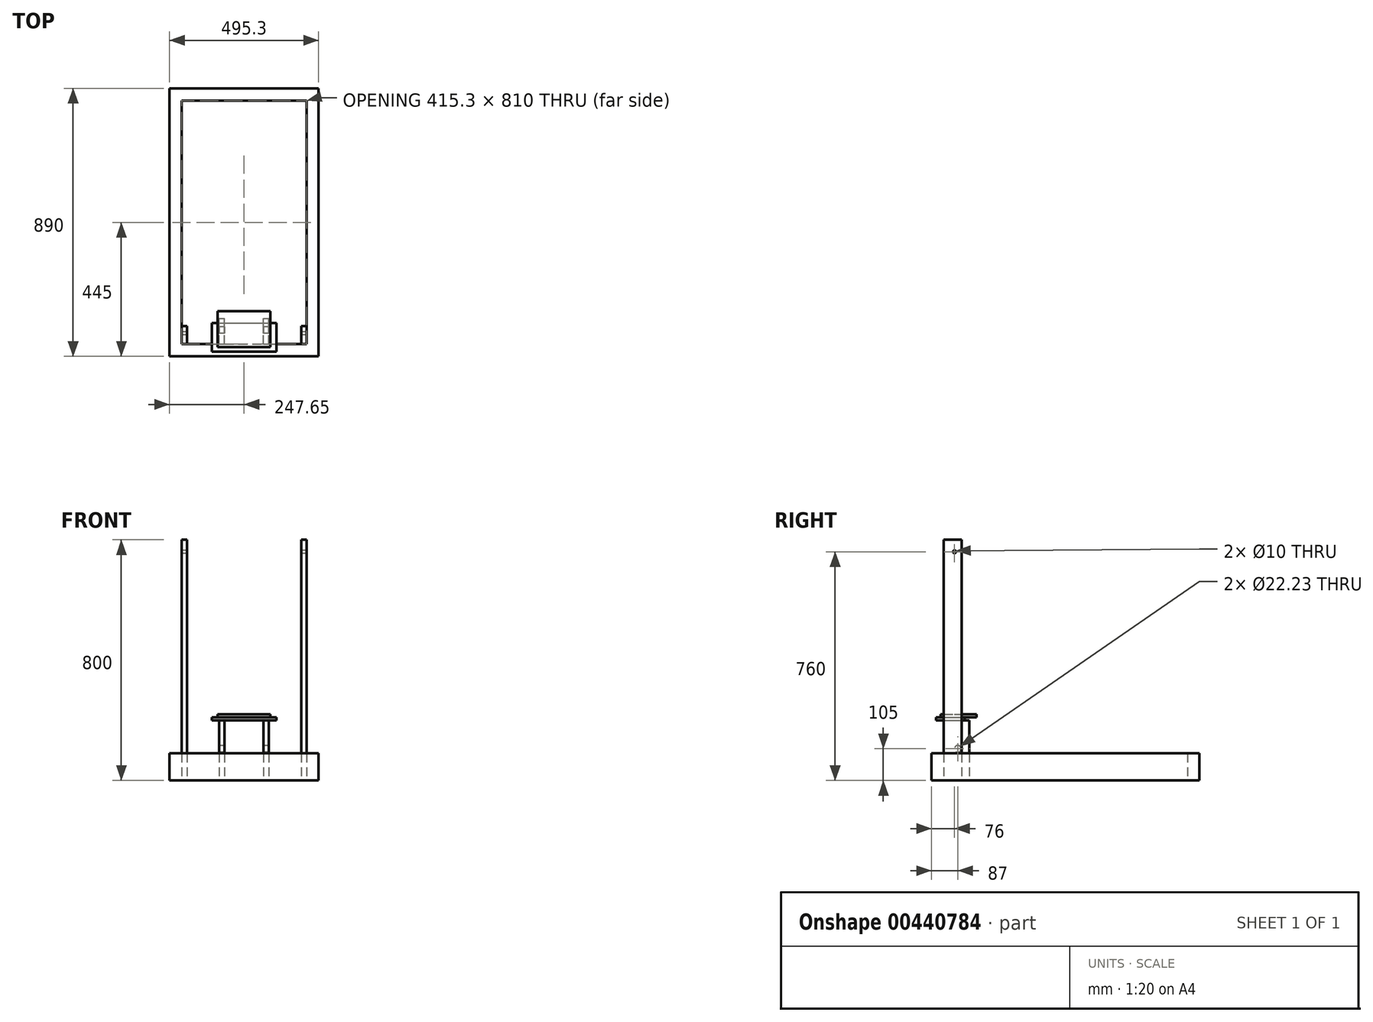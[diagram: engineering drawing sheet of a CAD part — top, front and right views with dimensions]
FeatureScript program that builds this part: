
annotation { "Feature Type Name" : "Feature", "Feature Type Description" : "" }
export const myFeature = defineFeature(function(context is Context, id is Id, definition is map)
    precondition{}
    {
        {
            var Q0;
            Q0=qCreatedBy(makeId("Top.planeOp"),FACE);
            var sketch = newSketch(context, id + "F0", { "sketchPlane" : qUnion([Q0])});
            skLineSegment(sketch, "E0.bottom", {"start": v(0, 0) * mm, "end": v(495.3, 0) * mm});
            skLineSegment(sketch, "E0.top", {"start": v(0, 890) * mm, "end": v(495.3, 890) * mm});
            skLineSegment(sketch, "E0.left", {"start": v(0, 0) * mm, "end": v(0, 890) * mm});
            skLineSegment(sketch, "E0.right", {"start": v(495.3, 0) * mm, "end": v(495.3, 890) * mm});
            skLineSegment(sketch, "E1.bottom", {"start": v(40, 40) * mm, "end": v(455.3, 40) * mm});
            skLineSegment(sketch, "E1.top", {"start": v(40, 850) * mm, "end": v(455.3, 850) * mm});
            skLineSegment(sketch, "E1.left", {"start": v(40, 40) * mm, "end": v(40, 850) * mm});
            skLineSegment(sketch, "E1.right", {"start": v(455.3, 40) * mm, "end": v(455.3, 850) * mm});
            skSolve(sketch);
        }
        {
            var Q0;
            Q0 = qSketchRegion(id + "F0", true);
            extrude(context, id + "F1", {"entities" : qUnion([Q0]), "depth" : 90 * mm});
        }
        {
            var Q0;
            Q0=qCreatedBy(makeId("Top.planeOp"),FACE);
            var sketch = newSketch(context, id + "F2", { "sketchPlane" : qUnion([Q0])});
            skLineSegment(sketch, "E2.bottom", {"start": v(165, 40) * mm, "end": v(182.5, 40) * mm});
            skLineSegment(sketch, "E2.top", {"start": v(165, 125) * mm, "end": v(182.5, 125) * mm});
            skLineSegment(sketch, "E2.left", {"start": v(165, 40) * mm, "end": v(165, 125) * mm});
            skLineSegment(sketch, "E2.right", {"start": v(182.5, 40) * mm, "end": v(182.5, 125) * mm});
            skLineSegment(sketch, "E3.bottom", {"start": v(312.3, 40) * mm, "end": v(330.3, 40) * mm});
            skLineSegment(sketch, "E3.top", {"start": v(312.3, 125) * mm, "end": v(330.3, 125) * mm});
            skLineSegment(sketch, "E3.left", {"start": v(330.3, 40) * mm, "end": v(330.3, 125) * mm});
            skLineSegment(sketch, "E3.right", {"start": v(312.3, 40) * mm, "end": v(312.3, 125) * mm});
            skSolve(sketch);
        }
        {
            var Q0;
            Q0=makeQuery(id+"F2.imprint","IMPRINT",FACE,{"disambiguationData":[TD([[makeQuery(id+"F2.imprint","IMPRINT",EDGE,{"derivedFrom":sQuery(id+"F2.wireOp",EDGE,"E2.bottom")}),1.0]])]});
            var Q1;
            Q1=makeQuery(id+"F2.imprint","IMPRINT",FACE,{"disambiguationData":[TD([[makeQuery(id+"F2.imprint","IMPRINT",EDGE,{"derivedFrom":sQuery(id+"F2.wireOp",EDGE,"E3.bottom")}),1.0]])]});
            extrude(context, id + "F3", {"entities" : qUnion([Q0, Q1]), "operationType" : NewBodyOperationType.ADD, "depth" : 200 * mm});
        }
        {
            var Q0;
            Q0=qCreatedBy(makeId("Top.planeOp"),FACE);
            var sketch = newSketch(context, id + "F4", { "sketchPlane" : qUnion([Q0])});
            skLineSegment(sketch, "E4.bottom", {"start": v(40, 40) * mm, "end": v(57.5, 40) * mm});
            skLineSegment(sketch, "E4.top", {"start": v(40, 100) * mm, "end": v(57.5, 100) * mm});
            skLineSegment(sketch, "E4.left", {"start": v(40, 40) * mm, "end": v(40, 100) * mm});
            skLineSegment(sketch, "E4.right", {"start": v(57.5, 40) * mm, "end": v(57.5, 100) * mm});
            skLineSegment(sketch, "E5.bottom", {"start": v(437.3, 40) * mm, "end": v(455.3, 40) * mm});
            skLineSegment(sketch, "E5.top", {"start": v(437.3, 100) * mm, "end": v(455.3, 100) * mm});
            skLineSegment(sketch, "E5.left", {"start": v(437.3, 40) * mm, "end": v(437.3, 100) * mm});
            skLineSegment(sketch, "E5.right", {"start": v(455.3, 40) * mm, "end": v(455.3, 100) * mm});
            skSolve(sketch);
        }
        {
            var Q0;
            Q0=makeQuery(id+"F4.imprint","IMPRINT",FACE,{"disambiguationData":[TD([[makeQuery(id+"F4.imprint","IMPRINT",EDGE,{"derivedFrom":sQuery(id+"F4.wireOp",EDGE,"E4.bottom")}),1.0]])]});
            var Q1;
            Q1=makeQuery(id+"F4.imprint","IMPRINT",FACE,{"disambiguationData":[TD([[makeQuery(id+"F4.imprint","IMPRINT",EDGE,{"derivedFrom":sQuery(id+"F4.wireOp",EDGE,"E5.bottom")}),1.0]])]});
            extrude(context, id + "F5", {"entities" : qUnion([Q0, Q1]), "operationType" : NewBodyOperationType.ADD, "depth" : 800 * mm});
        }
        {
            var Q0;
            Q0=makeQuery(id+"F5.opExtrude","SWEPT_FACE",FACE,{"disambiguationData":[OSD([sQuery(id+"F4.wireOp",EDGE,"E4.left")])]});
            var sketch = newSketch(context, id + "F6", { "sketchPlane" : qUnion([Q0])});
            skCircle(sketch, "E6", {"center": v(-76, 760) * mm, "radius": 5 * mm});
            skSolve(sketch);
        }
        {
            var Q0;
            Q0 = qSketchRegion(id + "F6", true);
            extrude(context, id + "F7", {"entities" : qUnion([Q0]), "operationType" : NewBodyOperationType.REMOVE, "oppositeDirection" : true, "depth" : 453 * mm});
        }
        {
            var Q0;
            Q0=makeQuery(id+"F3.opExtrude","SWEPT_FACE",FACE,{"disambiguationData":[OSD([sQuery(id+"F2.wireOp",EDGE,"E2.left")])]});
            var sketch = newSketch(context, id + "F8", { "sketchPlane" : qUnion([Q0])});
            skCircle(sketch, "E7", {"center": v(-87, 105) * mm, "radius": 11.11 * mm});
            skSolve(sketch);
        }
        {
            var Q0;
            Q0 = qSketchRegion(id + "F8", true);
            extrude(context, id + "F9", {"entities" : qUnion([Q0]), "operationType" : NewBodyOperationType.REMOVE, "oppositeDirection" : true, "depth" : 184 * mm});
        }
        {
            var Q0;
            Q0=makeQuery(id+"F3.opExtrude","CAP_FACE",FACE,{"disambiguationData":[OSD([sQuery(id+"F2.wireOp",EDGE,"E2.bottom"),sQuery(id+"F2.wireOp",EDGE,"E2.top"),sQuery(id+"F2.wireOp",EDGE,"E2.left"),sQuery(id+"F2.wireOp",EDGE,"E2.right")])],"isStart":false});
            var sketch = newSketch(context, id + "F10", { "sketchPlane" : qUnion([Q0])});
            skLineSegment(sketch, "E8.bottom", {"start": v(140, 15) * mm, "end": v(355, 15) * mm});
            skLineSegment(sketch, "E8.top", {"start": v(140, 110) * mm, "end": v(355, 110) * mm});
            skLineSegment(sketch, "E8.left", {"start": v(140, 15) * mm, "end": v(140, 110) * mm});
            skLineSegment(sketch, "E8.right", {"start": v(355, 15) * mm, "end": v(355, 110) * mm});
            skSolve(sketch);
        }
        {
            var Q0;
            Q0 = qSketchRegion(id + "F10", true);
            extrude(context, id + "F11", {"entities" : qUnion([Q0]), "operationType" : NewBodyOperationType.ADD, "depth" : 10 * mm});
        }
        {
            var Q0;
            Q0=makeQuery(id+"F11.opExtrude","CAP_FACE",FACE,{"disambiguationData":[OSD([sQuery(id+"F10.wireOp",EDGE,"E8.bottom"),sQuery(id+"F10.wireOp",EDGE,"E8.top"),sQuery(id+"F10.wireOp",EDGE,"E8.left"),sQuery(id+"F10.wireOp",EDGE,"E8.right")])],"isStart":false});
            var sketch = newSketch(context, id + "F12", { "sketchPlane" : qUnion([Q0])});
            skLineSegment(sketch, "E9.bottom", {"start": v(335, 30) * mm, "end": v(160, 30) * mm});
            skLineSegment(sketch, "E9.top", {"start": v(335, 150) * mm, "end": v(160, 150) * mm});
            skLineSegment(sketch, "E9.left", {"start": v(335, 30) * mm, "end": v(335, 150) * mm});
            skLineSegment(sketch, "E9.right", {"start": v(160, 30) * mm, "end": v(160, 150) * mm});
            skSolve(sketch);
        }
        {
            var Q0;
            {var subQ0=sQuery(id+"F12.wireOp",EDGE,"E9.bottom");Q0=makeQuery(id+"F12.imprint","IMPRINT",FACE,{"disambiguationData":[TD([[makeQuery(id+"F12.imprint","IMPRINT",EDGE,{"derivedFrom":subQ0}),-1.0]])]});}
            var Q1;
            {var subQ0=sQuery(id+"F12.wireOp",EDGE,"E9.top");Q1=makeQuery(id+"F12.imprint","IMPRINT",FACE,{"disambiguationData":[TD([[makeQuery(id+"F12.imprint","IMPRINT",EDGE,{"derivedFrom":subQ0}),1.0]])]});}
            extrude(context, id + "F13", {"entities" : qUnion([Q0, Q1]), "operationType" : NewBodyOperationType.ADD, "depth" : 10 * mm});
        }
    });
